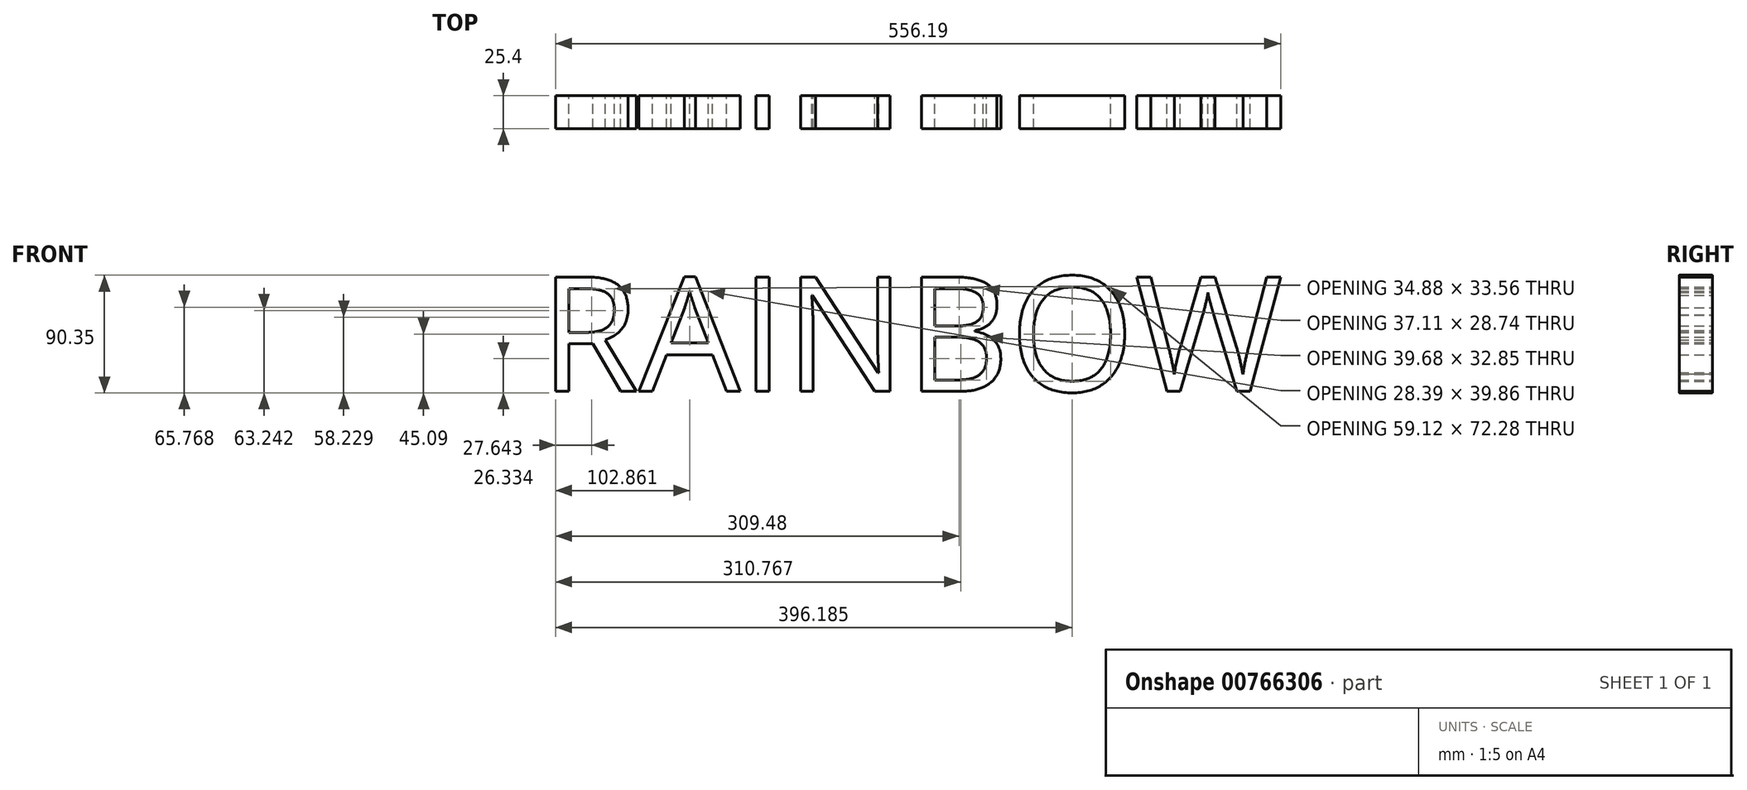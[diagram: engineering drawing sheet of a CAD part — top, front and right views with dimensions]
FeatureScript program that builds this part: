
annotation { "Feature Type Name" : "Feature", "Feature Type Description" : "" }
export const myFeature = defineFeature(function(context is Context, id is Id, definition is map)
    precondition{}
    {
        {
            var Q0;
            Q0=qCreatedBy(makeId("Front.planeOp"),FACE);
            var sketch = newSketch(context, id + "F0", { "sketchPlane" : qUnion([Q0])});
            skText(sketch, "E0", { "text": "RAINBOW", "fontName": "OpenSans-Regular.ttf"});
            const initialGuessF0  = {"E0": [-0.13243, -0.04857, 1, 0, 0.08851]};
            skSetInitialGuess(sketch, initialGuessF0);
            skSolve(sketch);
        }
        {
            var Q0;
            Q0 = qSketchRegion(id + "F0", true);
            extrude(context, id + "F1", {"entities" : qUnion([Q0]), "depth" : 25.4 * mm, "offsetDistance" : 25.4 * mm});
        }
    });
